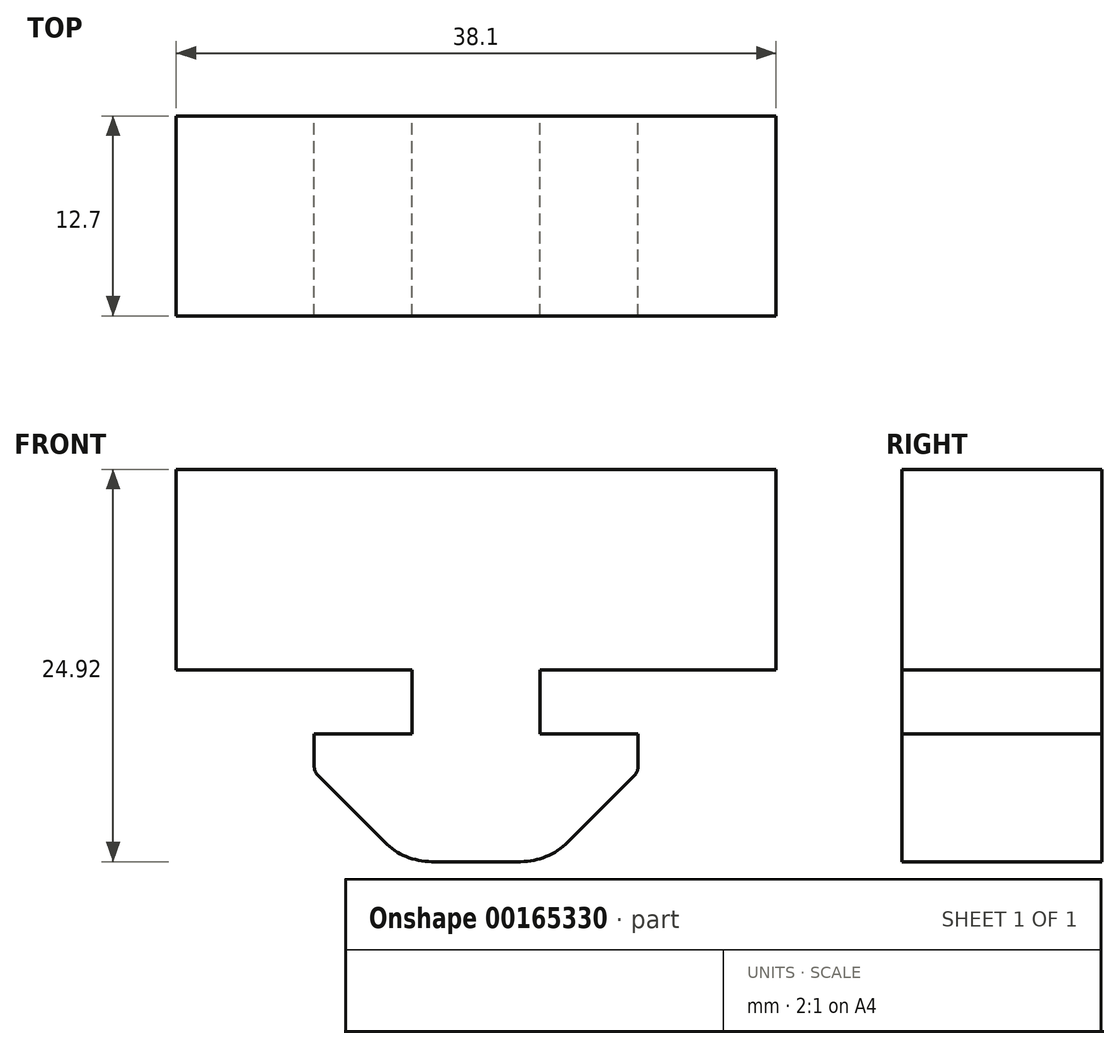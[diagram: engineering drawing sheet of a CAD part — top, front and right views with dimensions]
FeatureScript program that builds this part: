
annotation { "Feature Type Name" : "Feature", "Feature Type Description" : "" }
export const myFeature = defineFeature(function(context is Context, id is Id, definition is map)
    precondition{}
    {
        {
            var Q0;
            Q0=qCreatedBy(makeId("Front.planeOp"),FACE);
            var sketch = newSketch(context, id + "F0", { "sketchPlane" : qUnion([Q0])});
            skLineSegment(sketch, "E0", {"start": v(-37.76, 18.12) * mm, "end": v(-22.77, 18.12) * mm});
            skLineSegment(sketch, "E1", {"start": v(-22.77, 18.12) * mm, "end": v(-22.77, 14.06) * mm});
            skLineSegment(sketch, "E2", {"start": v(-22.77, 14.06) * mm, "end": v(-29, 14.06) * mm});
            skLineSegment(sketch, "E3", {"start": v(-29, 14.06) * mm, "end": v(-29, 12) * mm});
            skArc(sketch, "E4", {"start": v(-29, 12) * mm, "mid": v(-28.93, 11.66) * mm, "end": v(-28.73, 11.37) * mm});
            skArc(sketch, "E5", {"start": v(-24.53, 7.17) * mm, "mid": v(-23.16, 6.25) * mm, "end": v(-21.54, 5.93) * mm});
            skArc(sketch, "E6", {"start": v(-15.88, 5.93) * mm, "mid": v(-14.26, 6.25) * mm, "end": v(-12.88, 7.17) * mm});
            skArc(sketch, "E7", {"start": v(-8.68, 11.37) * mm, "mid": v(-8.49, 11.66) * mm, "end": v(-8.42, 12) * mm});
            skLineSegment(sketch, "E8", {"start": v(-28.73, 11.37) * mm, "end": v(-24.53, 7.17) * mm});
            skLineSegment(sketch, "E9", {"start": v(-21.54, 5.93) * mm, "end": v(-15.88, 5.93) * mm});
            skLineSegment(sketch, "E10", {"start": v(-12.88, 7.17) * mm, "end": v(-8.68, 11.37) * mm});
            skLineSegment(sketch, "E11", {"start": v(0.34, 18.12) * mm, "end": v(-14.64, 18.12) * mm});
            skLineSegment(sketch, "E12", {"start": v(-14.64, 18.12) * mm, "end": v(-14.64, 14.06) * mm});
            skLineSegment(sketch, "E13", {"start": v(-14.64, 14.06) * mm, "end": v(-8.42, 14.06) * mm});
            skLineSegment(sketch, "E14", {"start": v(-37.76, 18.12) * mm, "end": v(-37.76, 30.85) * mm});
            skLineSegment(sketch, "E15", {"start": v(-37.76, 30.85) * mm, "end": v(0.34, 30.85) * mm});
            skLineSegment(sketch, "E16", {"start": v(0.34, 30.85) * mm, "end": v(0.34, 18.12) * mm});
            skLineSegment(sketch, "E17", {"start": v(-8.42, 12) * mm, "end": v(-8.42, 14.06) * mm});
            skSolve(sketch);
        }
        {
            var Q0;
            Q0 = qSketchRegion(id + "F0", true);
            extrude(context, id + "F1", {"entities" : qUnion([Q0]), "depth" : 12.7 * mm});
        }
    });
